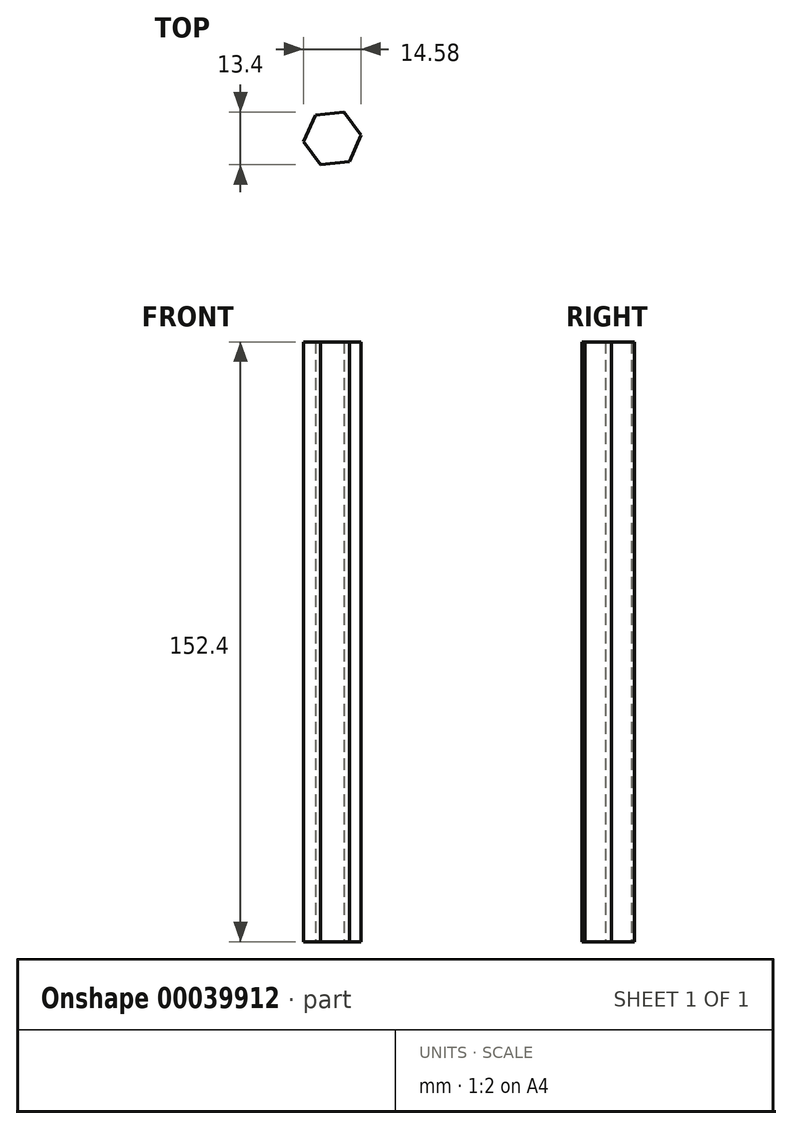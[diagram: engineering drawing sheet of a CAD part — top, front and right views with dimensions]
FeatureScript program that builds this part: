
annotation { "Feature Type Name" : "Feature", "Feature Type Description" : "" }
export const myFeature = defineFeature(function(context is Context, id is Id, definition is map)
    precondition{}
    {
        {
            var Q0;
            Q0=qCreatedBy(makeId("Top.planeOp"),FACE);
            var sketch = newSketch(context, id + "F0", { "sketchPlane" : qUnion([Q0])});
            skCircle(sketch, "E0.cCircle", {"center": v(0, 0) * mm, "radius": 6.35 * mm, "construction": true});
            skLineSegment(sketch, "E0.0", {"start": v(2.98, 6.7) * mm, "end": v(7.3, 0.77) * mm});
            skLineSegment(sketch, "E0.1", {"start": v(7.3, 0.77) * mm, "end": v(4.31, -5.93) * mm});
            skLineSegment(sketch, "E0.2", {"start": v(4.31, -5.93) * mm, "end": v(-2.98, -6.7) * mm});
            skLineSegment(sketch, "E0.3", {"start": v(-2.98, -6.7) * mm, "end": v(-7.3, -0.77) * mm});
            skLineSegment(sketch, "E0.4", {"start": v(-7.3, -0.77) * mm, "end": v(-4.31, 5.93) * mm});
            skLineSegment(sketch, "E0.5", {"start": v(-4.31, 5.93) * mm, "end": v(2.98, 6.7) * mm});
            skPoint(sketch, "E0.0.midPoint", {"position": v(5.13, 3.74) * mm});
            skSolve(sketch);
        }
        {
            var Q0;
            Q0=makeQuery(id+"F0.imprint","IMPRINT",FACE,{"disambiguationData":[TD([[makeQuery(id+"F0.imprint","IMPRINT",EDGE,{"derivedFrom":sQuery(id+"F0.wireOp",EDGE,"E0.0")}),-1.0]])]});
            extrude(context, id + "F1", {"entities" : qUnion([Q0]), "depth" : 152.4 * mm});
        }
    });
